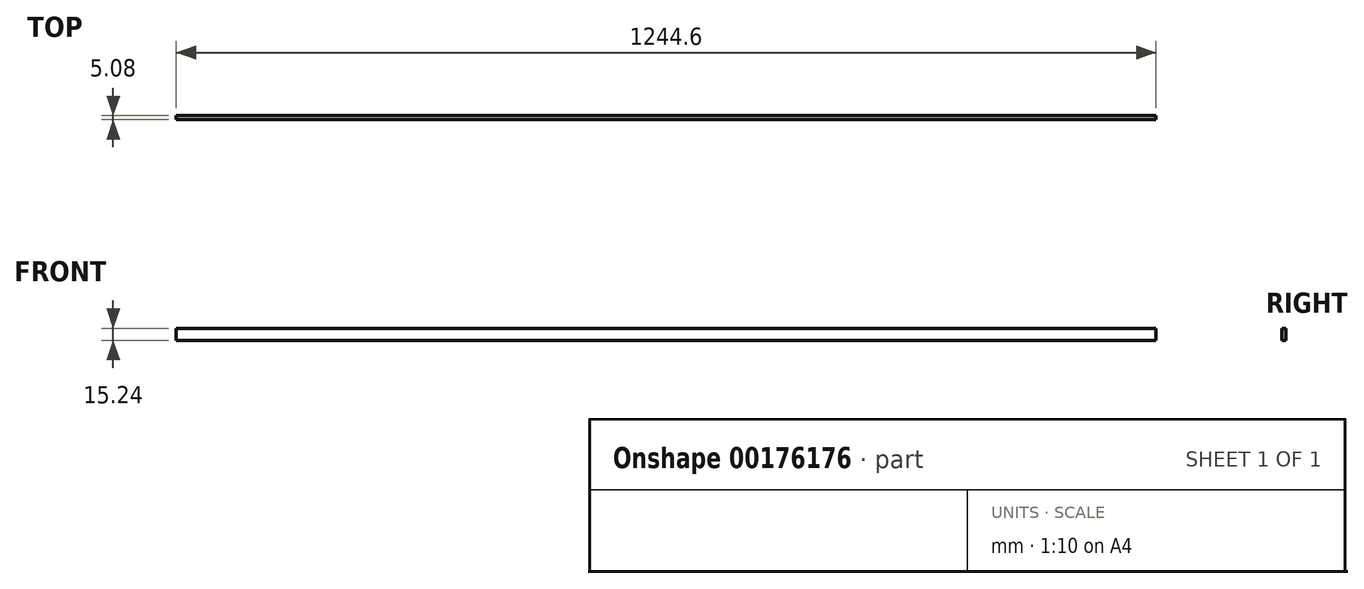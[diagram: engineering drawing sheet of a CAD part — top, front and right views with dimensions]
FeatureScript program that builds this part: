
annotation { "Feature Type Name" : "Feature", "Feature Type Description" : "" }
export const myFeature = defineFeature(function(context is Context, id is Id, definition is map)
    precondition{}
    {
        {
            var Q0;
            Q0=qCreatedBy(makeId("Front.planeOp"),FACE);
            var sketch = newSketch(context, id + "F0", { "sketchPlane" : qUnion([Q0])});
            skLineSegment(sketch, "E0.bottom", {"start": v(-622.3, 7.62) * mm, "end": v(622.3, 7.62) * mm});
            skLineSegment(sketch, "E0.top", {"start": v(-622.3, -7.62) * mm, "end": v(622.3, -7.62) * mm});
            skLineSegment(sketch, "E0.left", {"start": v(-622.3, 7.62) * mm, "end": v(-622.3, -7.62) * mm});
            skLineSegment(sketch, "E0.right", {"start": v(622.3, 7.62) * mm, "end": v(622.3, -7.62) * mm});
            skPoint(sketch, "E0.middle", {"position": v(0, 0) * mm});
            skSolve(sketch);
        }
        {
            var Q0;
            Q0=makeQuery(id+"F0.imprint","IMPRINT",FACE,{"disambiguationData":[TD([[makeQuery(id+"F0.imprint","IMPRINT",EDGE,{"derivedFrom":sQuery(id+"F0.wireOp",EDGE,"E0.bottom")}),-1.0]])]});
            extrude(context, id + "F1", {"entities" : qUnion([Q0]), "depth" : 5.08 * mm});
        }
    });
